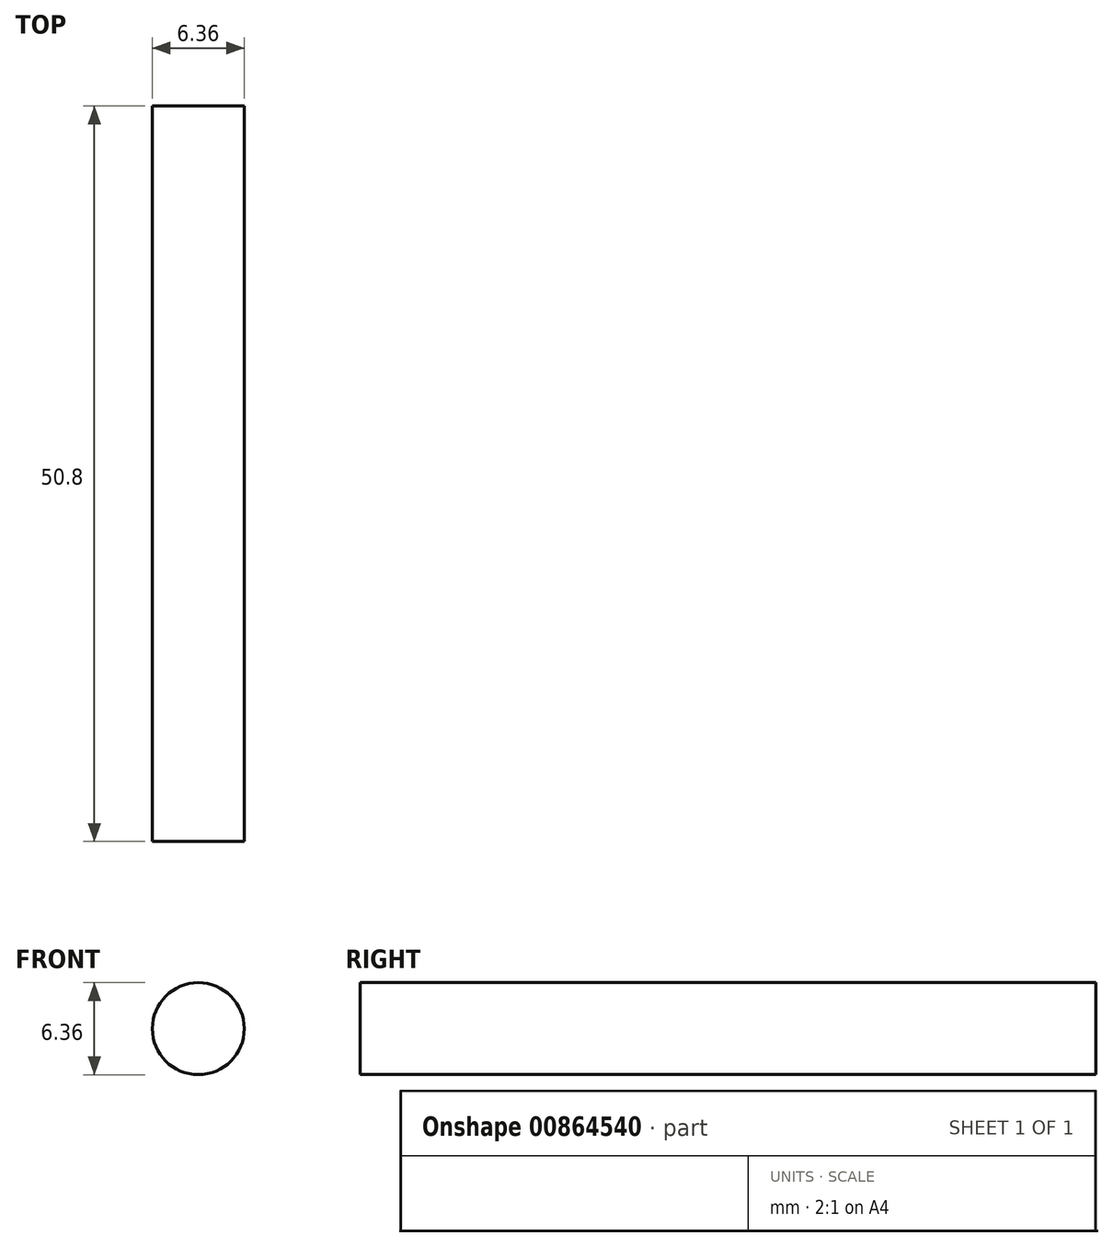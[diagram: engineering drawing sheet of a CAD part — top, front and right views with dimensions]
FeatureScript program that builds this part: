
annotation { "Feature Type Name" : "Feature", "Feature Type Description" : "" }
export const myFeature = defineFeature(function(context is Context, id is Id, definition is map)
    precondition{}
    {
        {
            var Q0;
            Q0=qCreatedBy(makeId("Front.planeOp"),FACE);
            var sketch = newSketch(context, id + "F0", { "sketchPlane" : qUnion([Q0])});
            skCircle(sketch, "E0", {"center": v(0, 0) * mm, "radius": 3.18 * mm});
            skSolve(sketch);
        }
        {
            var Q0;
            Q0=makeQuery(id+"F0.imprint","IMPRINT",FACE,{"disambiguationData":[TD([[makeQuery(id+"F0.imprint","IMPRINT",EDGE,{"derivedFrom":sQuery(id+"F0.wireOp",EDGE,"E0")}),1.0]])]});
            extrude(context, id + "F1", {"entities" : qUnion([Q0]), "depth" : 50.8 * mm, "offsetDistance" : 25.4 * mm});
        }
    });
